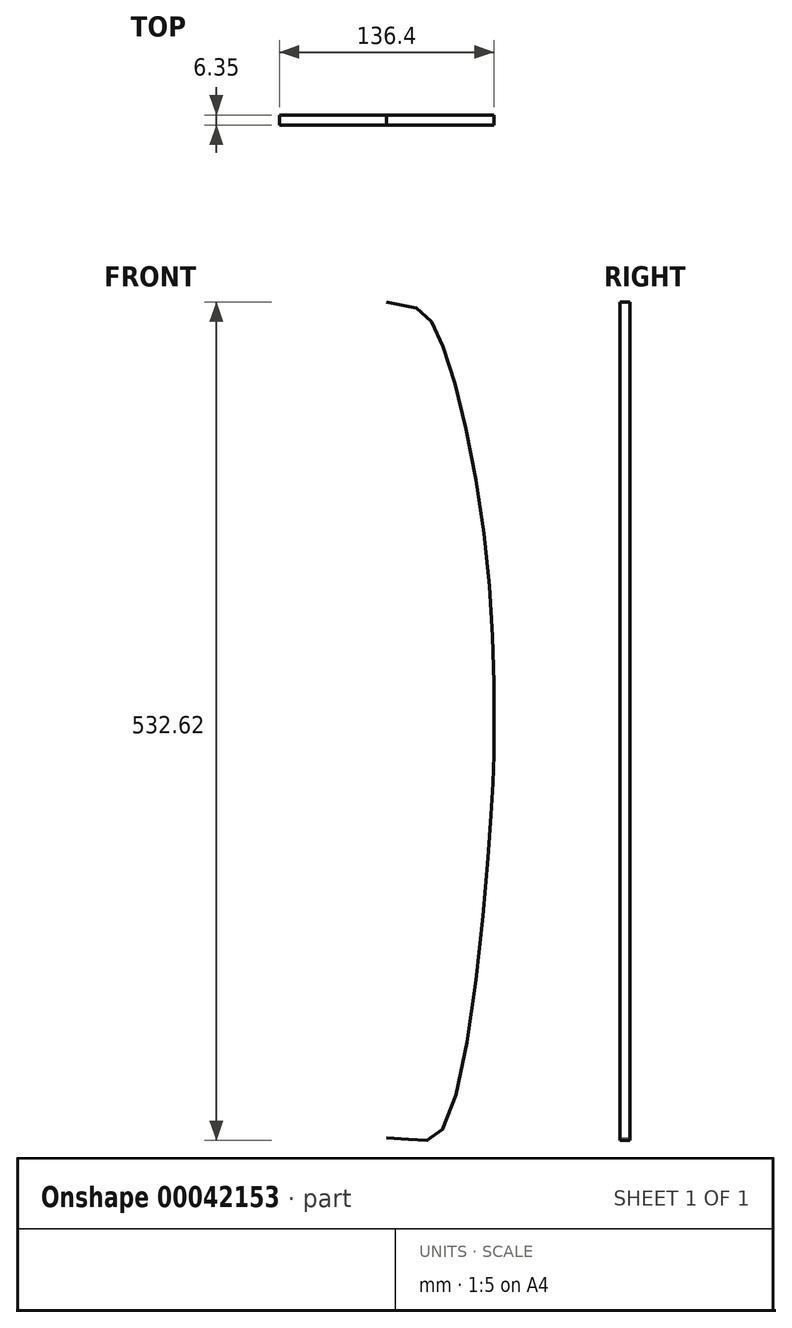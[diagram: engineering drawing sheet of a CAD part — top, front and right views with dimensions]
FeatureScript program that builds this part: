
annotation { "Feature Type Name" : "Feature", "Feature Type Description" : "" }
export const myFeature = defineFeature(function(context is Context, id is Id, definition is map)
    precondition{}
    {
        {
            var Q0;
            Q0=qCreatedBy(makeId("Front.planeOp"),FACE);
            var sketch = newSketch(context, id + "F0", { "sketchPlane" : qUnion([Q0])});
            skFitSpline(sketch, "E0", {"points": [v(0, 330.94) * mm, v(-31.16, 313.68) * mm, v(-61.16, 189.26) * mm, v(-68.14, 53.46) * mm, v(-65.04, -12.5) * mm, v(-34.78, -195.63) * mm, v(-16.15, -201.06) * mm, v(20.26, -198.84) * mm], "startDerivative": vector(-633.53, -58.93) * mm, "endDerivative": vector(438.6, 26.8) * mm});
            skFitSpline(sketch, "E1.MirrorCS", {"points": [v(0, 330.94) * mm, v(31.16, 313.68) * mm, v(61.16, 189.26) * mm, v(68.14, 53.46) * mm, v(65.04, -12.5) * mm, v(34.78, -195.63) * mm, v(16.15, -201.06) * mm, v(-20.26, -198.84) * mm], "startDerivative": vector(633.53, -58.93) * mm, "endDerivative": vector(-438.6, 26.8) * mm});
            skLineSegment(sketch, "E2.rect.bottom", {"start": v(15.72, 267.9) * mm, "end": v(-16.03, 267.9) * mm});
            skLineSegment(sketch, "E2.rect.top", {"start": v(15.72, 217.1) * mm, "end": v(-16.03, 217.1) * mm});
            skLineSegment(sketch, "E2.rect.left", {"start": v(15.72, 267.9) * mm, "end": v(15.72, 217.1) * mm});
            skLineSegment(sketch, "E2.rect.right", {"start": v(-16.03, 267.9) * mm, "end": v(-16.03, 217.1) * mm});
            skLineSegment(sketch, "E3", {"start": v(0, 330.94) * mm, "end": v(0, -190.29) * mm});
            skLineSegment(sketch, "E4.rect.bottom", {"start": v(15.87, -62.3) * mm, "end": v(-15.88, -62.3) * mm});
            skLineSegment(sketch, "E4.rect.left", {"start": v(15.87, -62.3) * mm, "end": v(15.87, -113.1) * mm});
            skLineSegment(sketch, "E4.rect.right", {"start": v(-15.88, -62.3) * mm, "end": v(-15.88, -113.1) * mm});
            skLineSegment(sketch, "E4.rect.top", {"start": v(15.87, -113.1) * mm, "end": v(-15.88, -113.1) * mm});
            skSolve(sketch);
        }
        {
            var Q0;
            {var subQ10=sQuery(id+"F0.wireOp",EDGE,"E2.rect.left");Q0=makeQuery(id+"F0.imprint","IMPRINT",FACE,{"disambiguationData":[TD([[makeQuery(id+"F0.imprint","IMPRINT",EDGE,{"derivedFrom":subQ10}),1.0]])]});}
            var Q1;
            {var subQ5=sQuery(id+"F0.wireOp",EDGE,"E2.rect.left");Q1=makeQuery(id+"F0.imprint","IMPRINT",FACE,{"disambiguationData":[TD([[makeQuery(id+"F0.imprint","IMPRINT",EDGE,{"derivedFrom":subQ5}),-1.0]])]});}
            var Q2;
            {var subQ5=sQuery(id+"F0.wireOp",EDGE,"E2.rect.right");Q2=makeQuery(id+"F0.imprint","IMPRINT",FACE,{"disambiguationData":[TD([[makeQuery(id+"F0.imprint","IMPRINT",EDGE,{"derivedFrom":subQ5}),1.0]])]});}
            var Q3;
            {var subQ3=sQuery(id+"F0.wireOp",EDGE,"E4.rect.right");Q3=makeQuery(id+"F0.imprint","IMPRINT",FACE,{"disambiguationData":[TD([[makeQuery(id+"F0.imprint","IMPRINT",EDGE,{"derivedFrom":subQ3}),1.0]])]});}
            var Q4;
            {var subQ3=sQuery(id+"F0.wireOp",EDGE,"E4.rect.left");Q4=makeQuery(id+"F0.imprint","IMPRINT",FACE,{"disambiguationData":[TD([[makeQuery(id+"F0.imprint","IMPRINT",EDGE,{"derivedFrom":subQ3}),-1.0]])]});}
            extrude(context, id + "F1", {"entities" : qUnion([Q0, Q1, Q2, Q3, Q4]), "depth" : 6.35 * mm});
        }
    });
